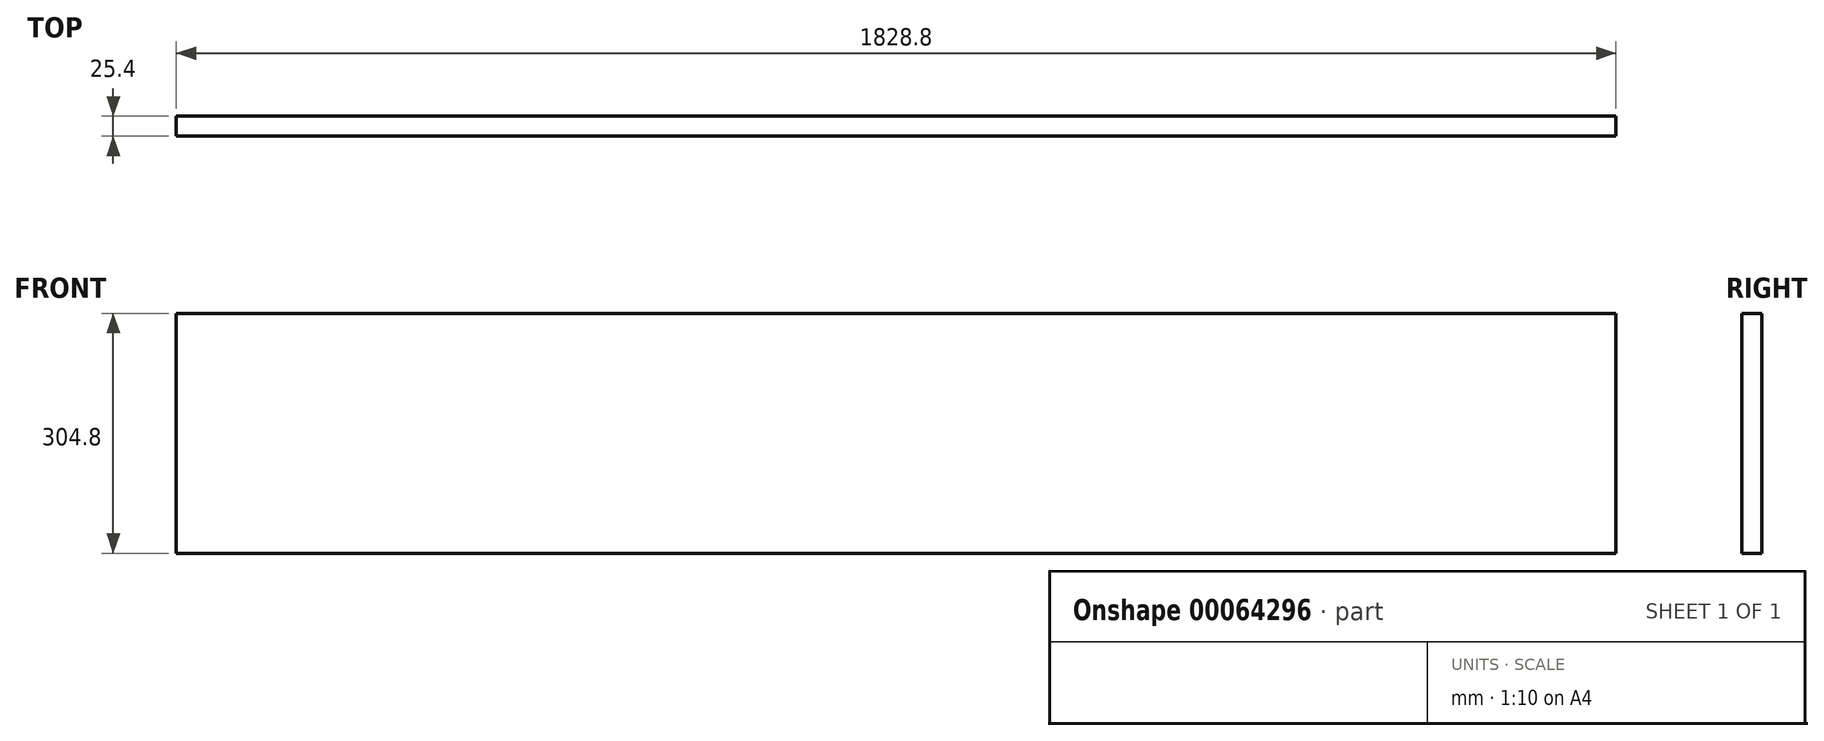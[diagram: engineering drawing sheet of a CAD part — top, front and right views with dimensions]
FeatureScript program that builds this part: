
annotation { "Feature Type Name" : "Feature", "Feature Type Description" : "" }
export const myFeature = defineFeature(function(context is Context, id is Id, definition is map)
    precondition{}
    {
        {
            var Q0;
            Q0=qCreatedBy(makeId("Front.planeOp"),FACE);
            var sketch = newSketch(context, id + "F0", { "sketchPlane" : qUnion([Q0])});
            skLineSegment(sketch, "E0.bottom", {"start": v(-914.4, -152.4) * mm, "end": v(914.4, -152.4) * mm});
            skLineSegment(sketch, "E0.top", {"start": v(-914.4, 152.4) * mm, "end": v(914.4, 152.4) * mm});
            skLineSegment(sketch, "E0.left", {"start": v(-914.4, -152.4) * mm, "end": v(-914.4, 152.4) * mm});
            skLineSegment(sketch, "E0.right", {"start": v(914.4, -152.4) * mm, "end": v(914.4, 152.4) * mm});
            skLineSegment(sketch, "E1.bottom", {"start": v(991.34, 542.1) * mm, "end": v(867.38, 542.1) * mm});
            skLineSegment(sketch, "E1.top", {"start": v(991.34, 603.3) * mm, "end": v(867.38, 603.3) * mm});
            skLineSegment(sketch, "E1.left", {"start": v(991.34, 542.1) * mm, "end": v(991.34, 603.3) * mm});
            skLineSegment(sketch, "E1.right", {"start": v(867.38, 542.1) * mm, "end": v(867.38, 603.3) * mm});
            skLineSegment(sketch, "E2", {"start": v(-914.4, 0) * mm, "end": v(0, 0) * mm, "construction": true});
            skLineSegment(sketch, "E3", {"start": v(0, -152.4) * mm, "end": v(0, 0) * mm, "construction": true});
            skSolve(sketch);
        }
        {
            var Q0;
            Q0=makeQuery(id+"F0.imprint","IMPRINT",FACE,{"disambiguationData":[TD([[makeQuery(id+"F0.imprint","IMPRINT",EDGE,{"derivedFrom":sQuery(id+"F0.wireOp",EDGE,"E0.bottom")}),1.0]])]});
            extrude(context, id + "F1", {"entities" : qUnion([Q0]), "depth" : 25.4 * mm});
        }
    });
